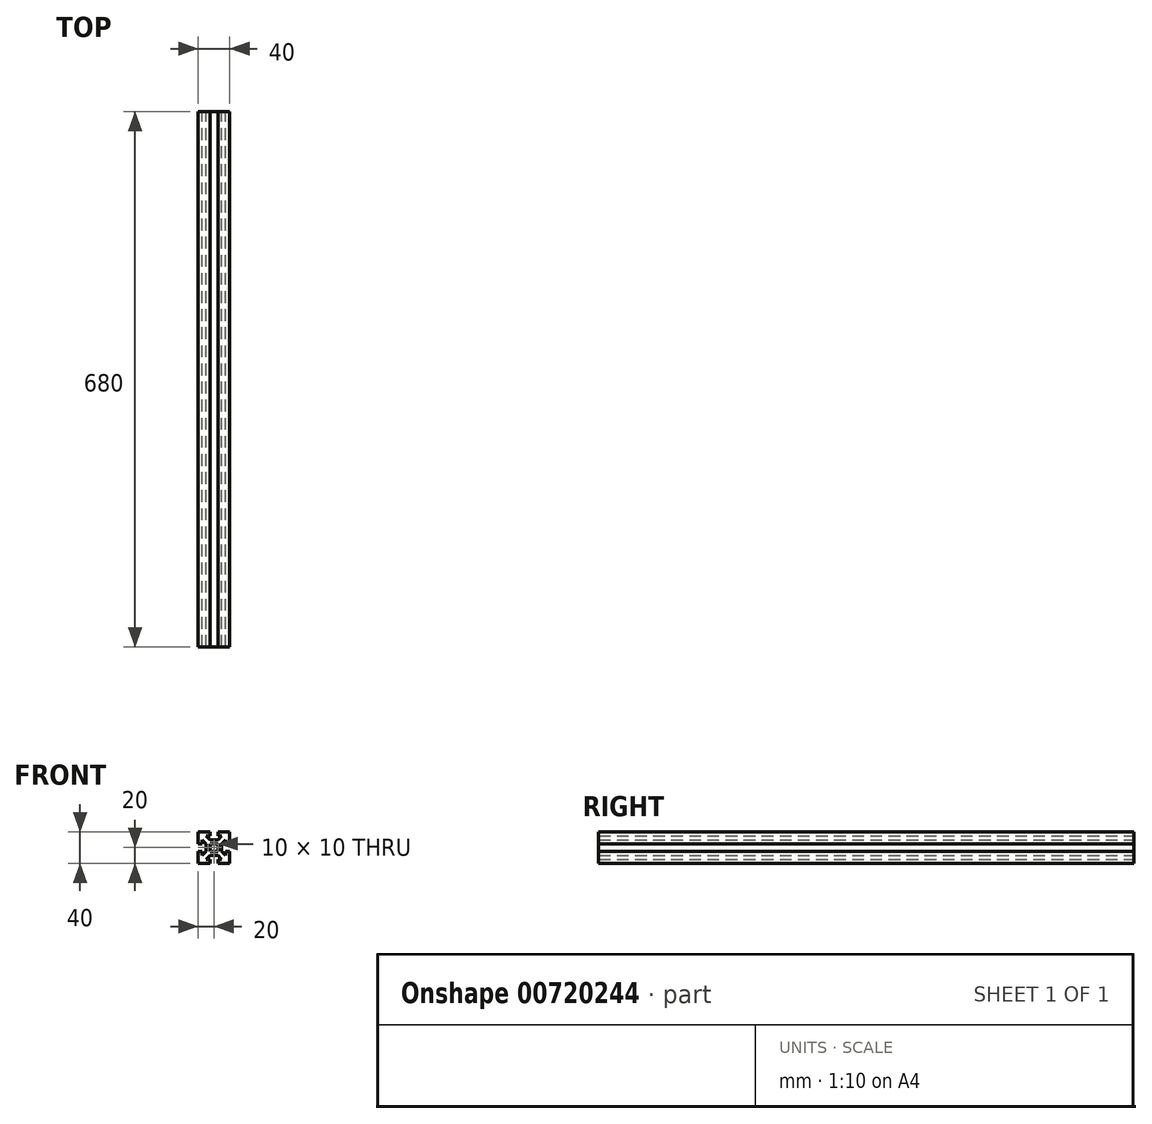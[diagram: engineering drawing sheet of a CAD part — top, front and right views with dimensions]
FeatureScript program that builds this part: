
annotation { "Feature Type Name" : "Feature", "Feature Type Description" : "" }
export const myFeature = defineFeature(function(context is Context, id is Id, definition is map)
    precondition{}
    {
        {
            var Q0;
            Q0=qCreatedBy(makeId("Front.planeOp"),FACE);
            var sketch = newSketch(context, id + "F0", { "sketchPlane" : qUnion([Q0])});
            skLineSegment(sketch, "E0.bottom", {"start": v(20, 20) * mm, "end": v(5, 20) * mm});
            skLineSegment(sketch, "E0.top", {"start": v(20, -20) * mm, "end": v(5, -20) * mm});
            skLineSegment(sketch, "E0.left", {"start": v(20, 20) * mm, "end": v(20, 5) * mm});
            skLineSegment(sketch, "E0.right", {"start": v(-20, 20) * mm, "end": v(-20, 5) * mm});
            skPoint(sketch, "E0.middle", {"position": v(0, 0) * mm});
            skLineSegment(sketch, "E1", {"start": v(0, 20) * mm, "end": v(0, -20) * mm, "construction": true});
            skLineSegment(sketch, "E2", {"start": v(-20, 0) * mm, "end": v(20, 0) * mm, "construction": true});
            skLineSegment(sketch, "E3", {"start": v(-20, 5) * mm, "end": v(-15, 5) * mm});
            skLineSegment(sketch, "E4", {"start": v(-20, -5) * mm, "end": v(-15, -5) * mm});
            skLineSegment(sketch, "E5", {"start": v(-5, 20) * mm, "end": v(-5, 15) * mm});
            skLineSegment(sketch, "E6", {"start": v(5, 20) * mm, "end": v(5, 15) * mm});
            skLineSegment(sketch, "E7", {"start": v(-10, 15) * mm, "end": v(-5, 15) * mm});
            skLineSegment(sketch, "E8", {"start": v(-10, -15) * mm, "end": v(-5, -15) * mm});
            skLineSegment(sketch, "E9", {"start": v(15, 10) * mm, "end": v(15, 5) * mm});
            skLineSegment(sketch, "E10", {"start": v(-15, 10) * mm, "end": v(-10, 5) * mm});
            skLineSegment(sketch, "E11", {"start": v(-10, 15) * mm, "end": v(-5, 10) * mm});
            skLineSegment(sketch, "E12", {"start": v(-15, -10) * mm, "end": v(-10, -5) * mm});
            skLineSegment(sketch, "E13", {"start": v(-10, -15) * mm, "end": v(-5, -10) * mm});
            skLineSegment(sketch, "E14.trimOffspring", {"start": v(20, -5) * mm, "end": v(20, -20) * mm});
            skLineSegment(sketch, "E15.trimOffspring", {"start": v(-20, -5) * mm, "end": v(-20, -20) * mm});
            skLineSegment(sketch, "E16.trimOffspring", {"start": v(-5, -20) * mm, "end": v(-20, -20) * mm});
            skLineSegment(sketch, "E17.trimOffspring", {"start": v(-5, 20) * mm, "end": v(-20, 20) * mm});
            skLineSegment(sketch, "E18.trimOffspring", {"start": v(5, 15) * mm, "end": v(10, 15) * mm});
            skLineSegment(sketch, "E19.trimOffspring", {"start": v(-15, -5) * mm, "end": v(-15, -10) * mm});
            skLineSegment(sketch, "E20.trimOffspring", {"start": v(15, -5) * mm, "end": v(15, -10) * mm});
            skLineSegment(sketch, "E21.trimOffspring", {"start": v(5, -15) * mm, "end": v(10, -15) * mm});
            skLineSegment(sketch, "E22.trimOffspring", {"start": v(-5, 5) * mm, "end": v(-5, -5) * mm});
            skLineSegment(sketch, "E23.trimOffspring", {"start": v(5, 5) * mm, "end": v(5, -5) * mm});
            skLineSegment(sketch, "E24.trimOffspring", {"start": v(15, 5) * mm, "end": v(20, 5) * mm});
            skLineSegment(sketch, "E25.trimOffspring", {"start": v(15, -5) * mm, "end": v(20, -5) * mm});
            skLineSegment(sketch, "E26.trimOffspring", {"start": v(5, -15) * mm, "end": v(5, -20) * mm});
            skLineSegment(sketch, "E27.trimOffspring", {"start": v(-5, -15) * mm, "end": v(-5, -20) * mm});
            skLineSegment(sketch, "E28.trimOffspring", {"start": v(-5, -5) * mm, "end": v(5, -5) * mm});
            skLineSegment(sketch, "E29.trimOffspring", {"start": v(-5, 5) * mm, "end": v(5, 5) * mm});
            skLineSegment(sketch, "E30", {"start": v(10, 5) * mm, "end": v(10, -5) * mm});
            skLineSegment(sketch, "E31", {"start": v(-5, 10) * mm, "end": v(5, 10) * mm});
            skLineSegment(sketch, "E32", {"start": v(-10, 5) * mm, "end": v(-10, -5) * mm});
            skLineSegment(sketch, "E33", {"start": v(-5, -10) * mm, "end": v(5, -10) * mm});
            skLineSegment(sketch, "E34.trimOffspring", {"start": v(-15, 10) * mm, "end": v(-15, 5) * mm});
            skPoint(sketch, "E35.orphan", {"position": v(20, 15) * mm});
            skPoint(sketch, "E36.orphan", {"position": v(20, -15) * mm});
            skPoint(sketch, "E37.orphan", {"position": v(15, -20) * mm});
            skPoint(sketch, "E38.orphan", {"position": v(-15, -20) * mm});
            skLineSegment(sketch, "E39.trimOffspring", {"start": v(-5, 0) * mm, "end": v(0, -5) * mm});
            skLineSegment(sketch, "E40.trimOffspring", {"start": v(-5, 0) * mm, "end": v(0, 5) * mm});
            skLineSegment(sketch, "E41.trimOffspring", {"start": v(0, 5) * mm, "end": v(5, 0) * mm});
            skLineSegment(sketch, "E42.trimOffspring", {"start": v(5, 10) * mm, "end": v(10, 15) * mm});
            skLineSegment(sketch, "E43.trimOffspring", {"start": v(10, 5) * mm, "end": v(15, 10) * mm});
            skLineSegment(sketch, "E44.trimOffspring", {"start": v(10, -5) * mm, "end": v(15, -10) * mm});
            skLineSegment(sketch, "E45.trimOffspring", {"start": v(5, -10) * mm, "end": v(10, -15) * mm});
            skLineSegment(sketch, "E46.trimOffspring", {"start": v(0, -5) * mm, "end": v(5, 0) * mm});
            skSolve(sketch);
        }
        {
            var Q0;
            Q0=makeQuery(id+"F0.imprint","IMPRINT",FACE,{"disambiguationData":[TD([[makeQuery(id+"F0.imprint","IMPRINT",EDGE,{"derivedFrom":sQuery(id+"F0.wireOp",EDGE,"E0.bottom")}),1.0]])]});
            extrude(context, id + "F1", {"entities" : qUnion([Q0]), "depth" : 680 * mm, "offsetDistance" : 25 * mm});
        }
    });
